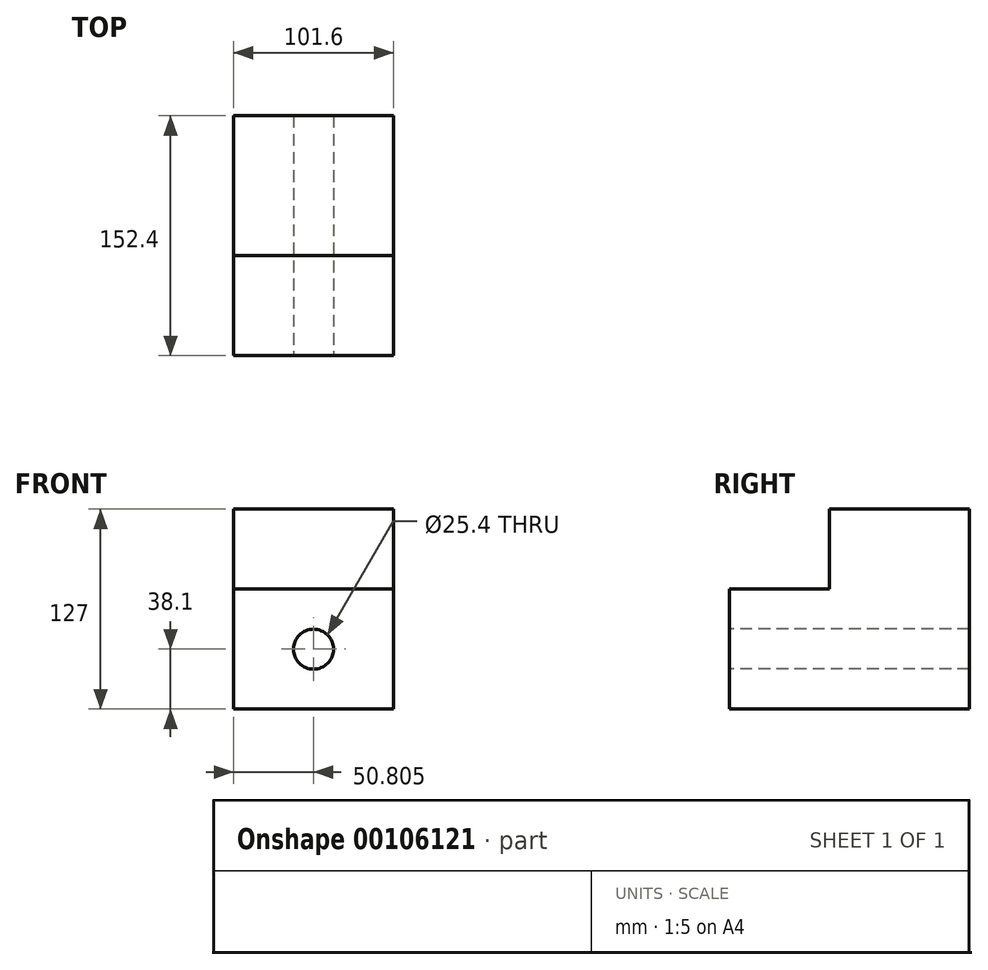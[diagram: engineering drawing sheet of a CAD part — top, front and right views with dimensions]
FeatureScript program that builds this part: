
annotation { "Feature Type Name" : "Feature", "Feature Type Description" : "" }
export const myFeature = defineFeature(function(context is Context, id is Id, definition is map)
    precondition{}
    {
        {
            var Q0;
            Q0=qCreatedBy(makeId("Top.planeOp"),FACE);
            var sketch = newSketch(context, id + "F0", { "sketchPlane" : qUnion([Q0])});
            skLineSegment(sketch, "E0.bottom", {"start": v(-58.03, 5.86) * mm, "end": v(43.57, 5.86) * mm});
            skLineSegment(sketch, "E0.top", {"start": v(-58.03, -146.54) * mm, "end": v(43.57, -146.54) * mm});
            skLineSegment(sketch, "E0.left", {"start": v(-58.03, 5.86) * mm, "end": v(-58.03, -146.54) * mm});
            skLineSegment(sketch, "E0.right", {"start": v(43.57, 5.86) * mm, "end": v(43.57, -146.54) * mm});
            skSolve(sketch);
        }
        {
            var Q0;
            Q0=makeQuery(id+"F0.imprint","IMPRINT",FACE,{"disambiguationData":[TD([[makeQuery(id+"F0.imprint","IMPRINT",EDGE,{"derivedFrom":sQuery(id+"F0.wireOp",EDGE,"E0.bottom")}),-1.0]])]});
            extrude(context, id + "F1", {"entities" : qUnion([Q0]), "depth" : 76.2 * mm});
        }
        {
            var Q0;
            Q0=makeQuery(id+"F1.opExtrude","CAP_FACE",FACE,{"disambiguationData":[OSD([sQuery(id+"F0.wireOp",EDGE,"E0.bottom"),sQuery(id+"F0.wireOp",EDGE,"E0.top"),sQuery(id+"F0.wireOp",EDGE,"E0.left"),sQuery(id+"F0.wireOp",EDGE,"E0.right")])],"isStart":false});
            var sketch = newSketch(context, id + "F2", { "sketchPlane" : qUnion([Q0])});
            skLineSegment(sketch, "E1.bottom", {"start": v(-58.03, 5.86) * mm, "end": v(43.57, 5.86) * mm});
            skLineSegment(sketch, "E1.top", {"start": v(-58.03, -83.04) * mm, "end": v(43.57, -83.04) * mm});
            skLineSegment(sketch, "E1.left", {"start": v(-58.03, 5.86) * mm, "end": v(-58.03, -83.04) * mm});
            skLineSegment(sketch, "E1.right", {"start": v(43.57, 5.86) * mm, "end": v(43.57, -83.04) * mm});
            skSolve(sketch);
        }
        {
            var Q0;
            Q0=makeQuery(id+"F2.imprint","IMPRINT",FACE,{"disambiguationData":[TD([[makeQuery(id+"F2.imprint","IMPRINT",EDGE,{"derivedFrom":sQuery(id+"F2.wireOp",EDGE,"E1.bottom")}),-1.0]])]});
            extrude(context, id + "F3", {"entities" : qUnion([Q0]), "operationType" : NewBodyOperationType.ADD, "depth" : 50.8 * mm});
        }
        {
            var Q0;
            Q0=makeQuery(id+"F1.opExtrude","SWEPT_FACE",FACE,{"disambiguationData":[OSD([sQuery(id+"F0.wireOp",EDGE,"E0.top")])]});
            var sketch = newSketch(context, id + "F4", { "sketchPlane" : qUnion([Q0])});
            skLineSegment(sketch, "E2.bottom", {"start": v(-58.03, 0) * mm, "end": v(-7.23, 0) * mm});
            skLineSegment(sketch, "E2.top", {"start": v(-58.03, 38.1) * mm, "end": v(-7.23, 38.1) * mm});
            skLineSegment(sketch, "E2.left", {"start": v(-58.03, 0) * mm, "end": v(-58.03, 38.1) * mm});
            skLineSegment(sketch, "E2.right", {"start": v(-7.23, 0) * mm, "end": v(-7.23, 38.1) * mm});
            skSolve(sketch);
        }
        {
            var Q0;
            Q0=sQuery(id+"F4.wireOp",VERTEX,"E2.top.end");
            var Q1;
            Q1=makeQuery(id+"F1.opExtrude","SWEPT_BODY",BODY,{"disambiguationData":[OSD([sQuery(id+"F0.wireOp",EDGE,"E0.bottom"),sQuery(id+"F0.wireOp",EDGE,"E0.top"),sQuery(id+"F0.wireOp",EDGE,"E0.left"),sQuery(id+"F0.wireOp",EDGE,"E0.right")])]});
            hole(context, id + "F5", {"style" : HoleStyle.SIMPLE, "endStyle" : HoleEndStyle.THROUGH, "holeDiameter" : 25.4 * mm, "locations" : qUnion([Q0]), "scope" : qUnion([Q1]), "isTappedThrough" : true});
        }
    });
